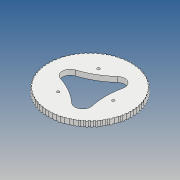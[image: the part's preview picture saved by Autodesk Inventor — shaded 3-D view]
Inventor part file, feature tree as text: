
AUTODESK INVENTOR PART (.ipt)
format: ipt  version: 2017 (Build 210142000, 142)  size: 358,400 bytes
history: native  units: mm
features: other x3, extrude x3, sketch x3
ambient origin geometry x8: Origin, YZ Plane, XZ Plane, XY Plane, X Axis, Y Axis, Z Axis, Center Point
bodies: Body1 (feature_tree)
feature tree (9):
  other  "Sólido1"
  extrude  "Extrusión1"  Depth=6.0mm TaperAngle=0.0deg
  extrude  "Extrusión2"  Depth=5.5mm
  extrude  "Extrusión3"  Depth=2.0mm
  sketch  "Boceto1"  dims[d0=98.708458mm d1=6.0mm d2=0.0mm]
  sketch  "Boceto2"  dims[d4=3.0mm d5=0.0mm d6=5.5mm]
  other  "Sólido2"
  sketch  "Boceto3"  dims[d7=3.0mm d8=0.0mm d9=2.0mm d11=72.0mm d20=43.43849mm d21=197.891213mm d22=65.335149mm d24=750.0mm d26=360.0deg d28=3.965979mm d30=83.0mm d31=3.0mm d32=2.0mm]
  other  "Sólido3"
